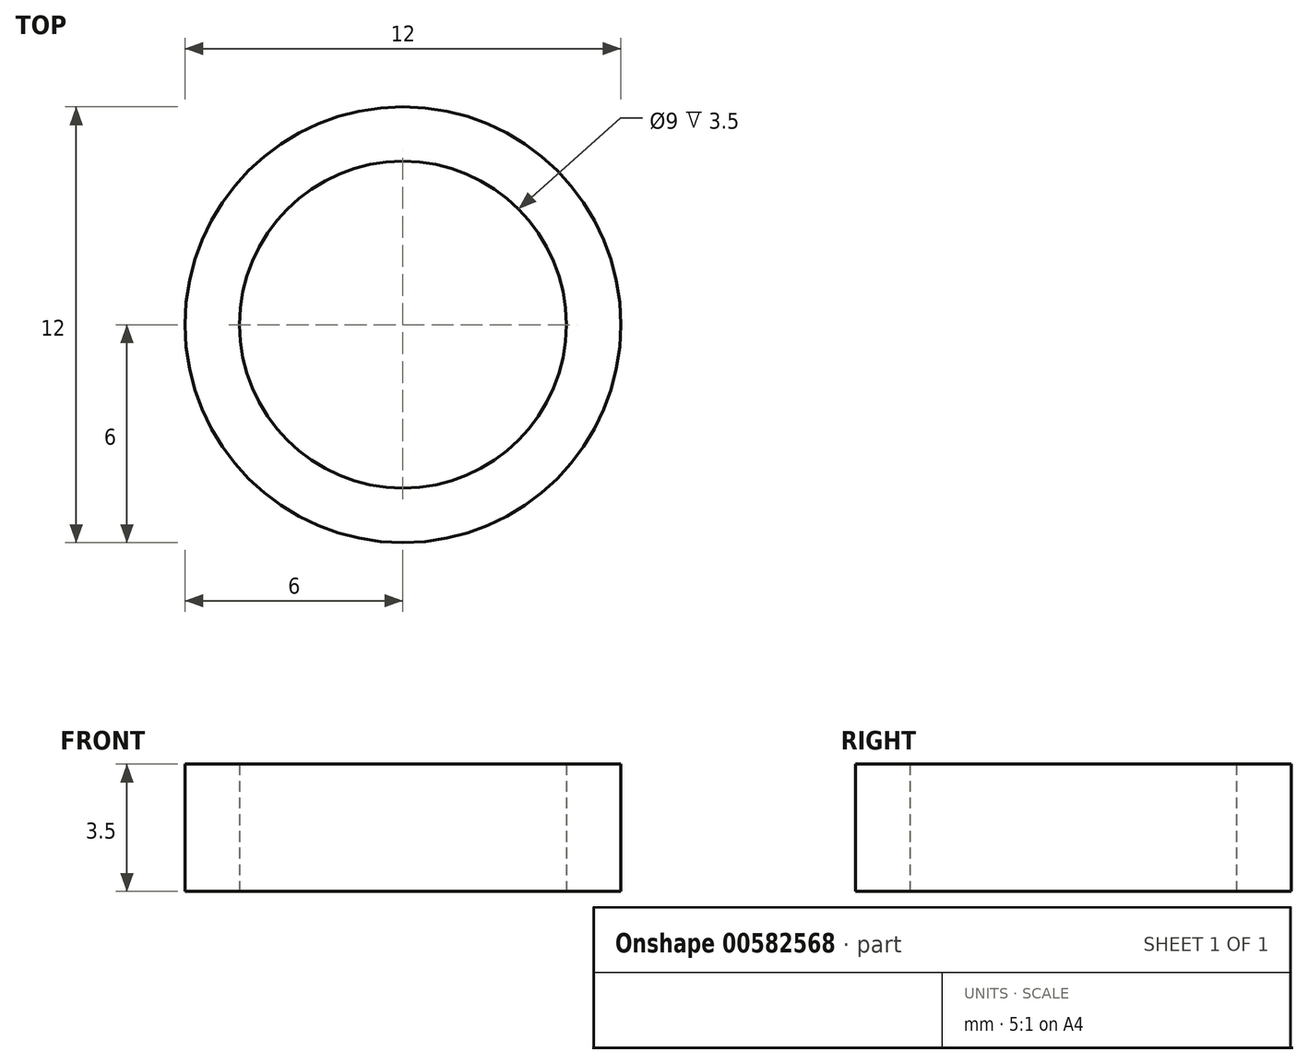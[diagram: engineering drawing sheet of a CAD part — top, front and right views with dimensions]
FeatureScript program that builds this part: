
annotation { "Feature Type Name" : "Feature", "Feature Type Description" : "" }
export const myFeature = defineFeature(function(context is Context, id is Id, definition is map)
    precondition{}
    {
        {
            var Q0;
            Q0=qCreatedBy(makeId("Top.planeOp"),FACE);
            var sketch = newSketch(context, id + "F0", { "sketchPlane" : qUnion([Q0])});
            skCircle(sketch, "E0", {"center": v(0, 0) * mm, "radius": 6 * mm});
            skCircle(sketch, "E1", {"center": v(0, 0) * mm, "radius": 4.5 * mm});
            skSolve(sketch);
        }
        {
            var Q0;
            Q0=makeQuery(id+"F0.imprint","IMPRINT",FACE,{"disambiguationData":[TD([[makeQuery(id+"F0.imprint","IMPRINT",EDGE,{"derivedFrom":sQuery(id+"F0.wireOp",EDGE,"E0")}),1.0]])]});
            extrude(context, id + "F1", {"entities" : qUnion([Q0]), "depth" : 3.5 * mm, "offsetDistance" : 25 * mm});
        }
    });
